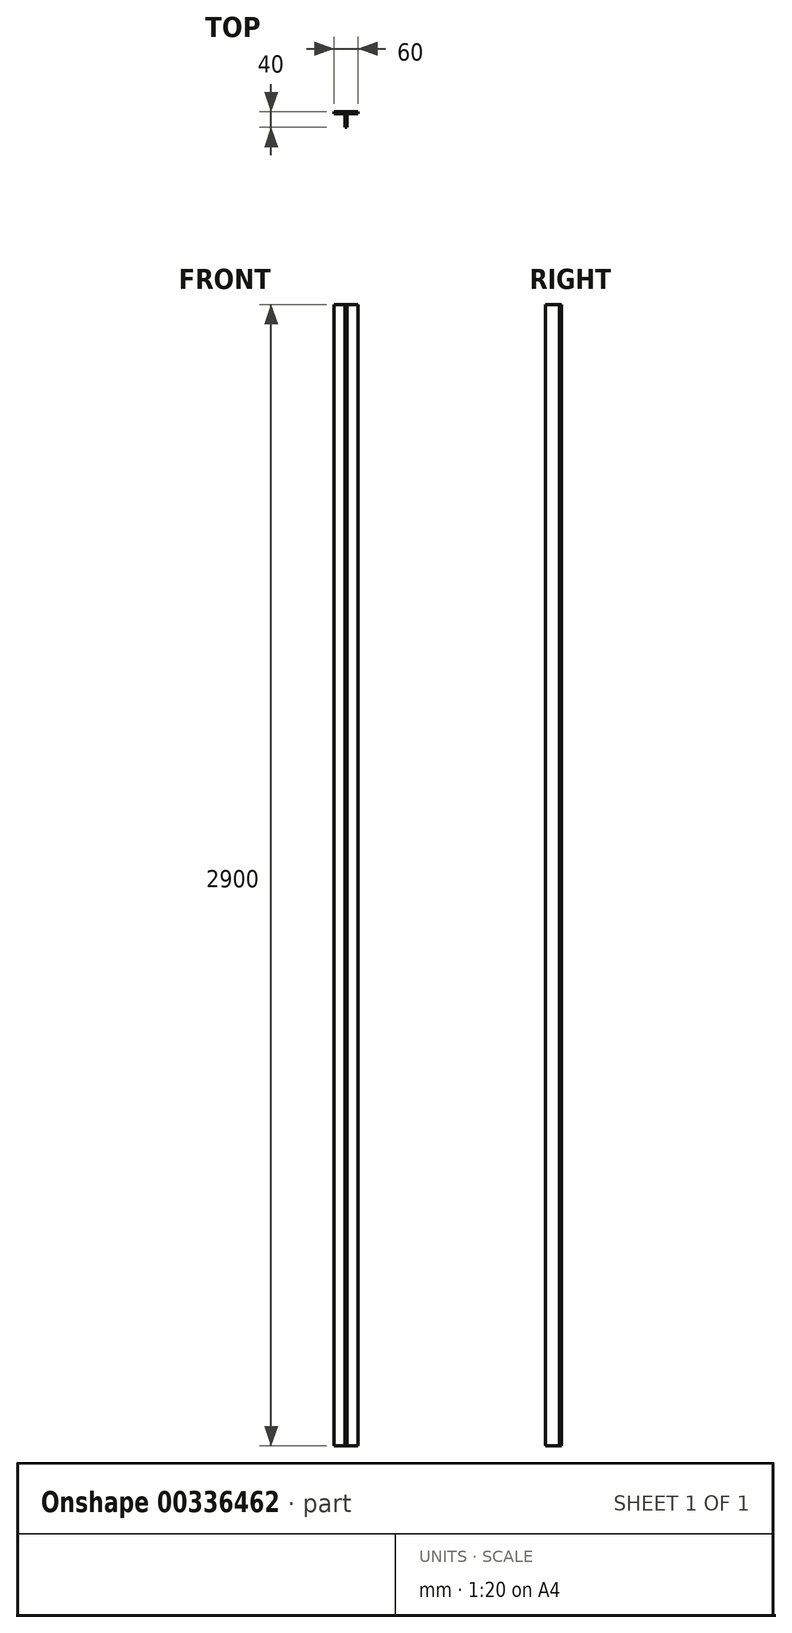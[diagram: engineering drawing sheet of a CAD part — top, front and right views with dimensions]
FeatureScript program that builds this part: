
annotation { "Feature Type Name" : "Feature", "Feature Type Description" : "" }
export const myFeature = defineFeature(function(context is Context, id is Id, definition is map)
    precondition{}
    {
        {
            var Q0;
            Q0=qCreatedBy(makeId("Top.planeOp"),FACE);
            var sketch = newSketch(context, id + "F0", { "sketchPlane" : qUnion([Q0])});
            skLineSegment(sketch, "E0", {"start": v(30, 0) * mm, "end": v(0, 0) * mm});
            skLineSegment(sketch, "E1", {"start": v(30, 0) * mm, "end": v(30, -5) * mm});
            skLineSegment(sketch, "E2", {"start": v(30, -5) * mm, "end": v(2.5, -5) * mm});
            skLineSegment(sketch, "E3", {"start": v(2.5, -5) * mm, "end": v(2.5, -40) * mm});
            skLineSegment(sketch, "E4", {"start": v(2.5, -40) * mm, "end": v(0, -40) * mm});
            skLineSegment(sketch, "E5.MirrorCS", {"start": v(-2.5, -40) * mm, "end": v(0, -40) * mm});
            skLineSegment(sketch, "E6.MirrorCS", {"start": v(-30, 0) * mm, "end": v(-30, -5) * mm});
            skLineSegment(sketch, "E7.MirrorCS", {"start": v(-2.5, -5) * mm, "end": v(-2.5, -40) * mm});
            skLineSegment(sketch, "E8.MirrorCS", {"start": v(-30, 0) * mm, "end": v(0, 0) * mm});
            skLineSegment(sketch, "E9.MirrorCS", {"start": v(-30, -5) * mm, "end": v(-2.5, -5) * mm});
            skSolve(sketch);
        }
        {
            var Q0;
            Q0=makeQuery(id+"F0.imprint","IMPRINT",FACE,{"disambiguationData":[TD([[makeQuery(id+"F0.imprint","IMPRINT",EDGE,{"derivedFrom":sQuery(id+"F0.wireOp",EDGE,"E0")}),1.0]])]});
            extrude(context, id + "F1", {"entities" : qUnion([Q0]), "depth" : 2900 * mm});
        }
    });
